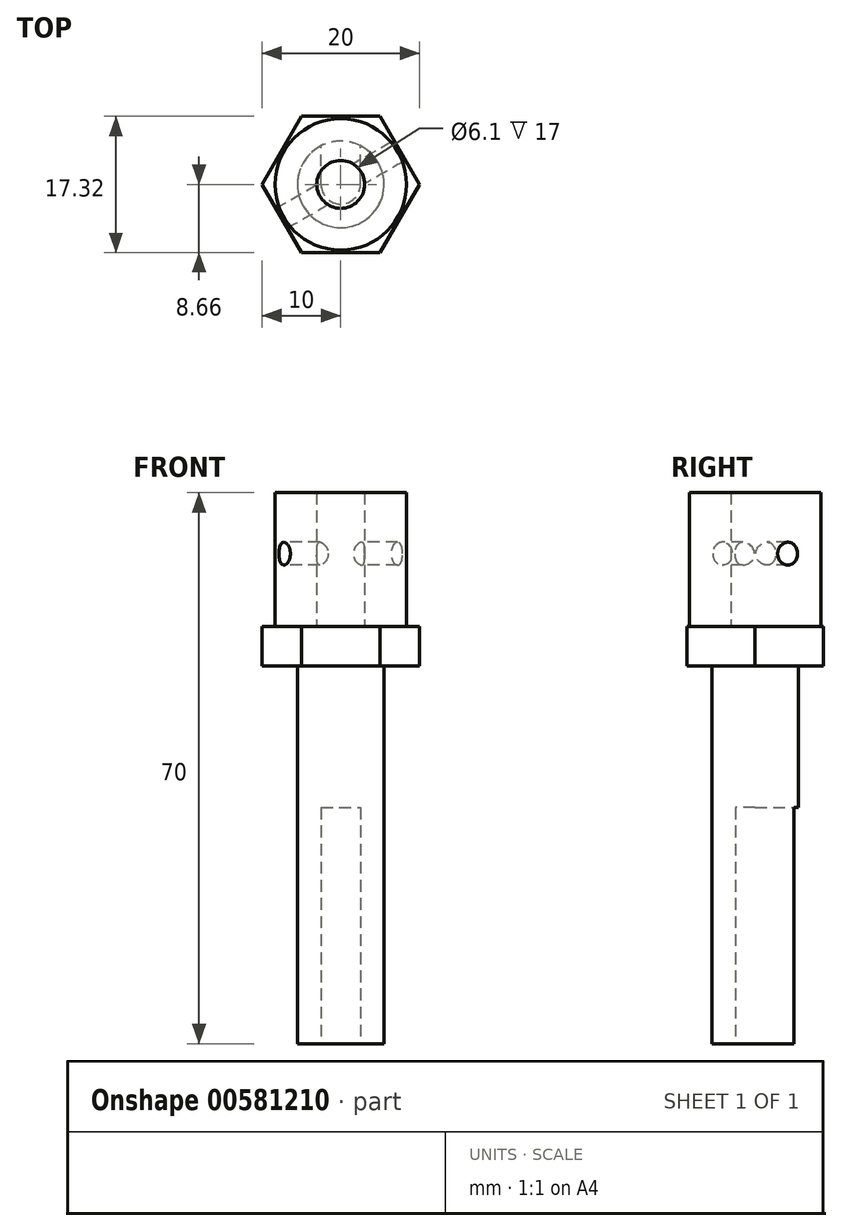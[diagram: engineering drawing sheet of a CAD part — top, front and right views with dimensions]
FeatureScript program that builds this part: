
annotation { "Feature Type Name" : "Feature", "Feature Type Description" : "" }
export const myFeature = defineFeature(function(context is Context, id is Id, definition is map)
    precondition{}
    {
        {
            var Q0;
            Q0=qCreatedBy(makeId("Top.planeOp"),FACE);
            var sketch = newSketch(context, id + "F0", { "sketchPlane" : qUnion([Q0])});
            skCircle(sketch, "E0.cCircle", {"center": v(0, 0) * mm, "radius": 8.66 * mm, "construction": true});
            skLineSegment(sketch, "E0.0", {"start": v(5, 8.66) * mm, "end": v(10, 0) * mm});
            skLineSegment(sketch, "E0.1", {"start": v(10, 0) * mm, "end": v(5, -8.66) * mm});
            skLineSegment(sketch, "E0.2", {"start": v(5, -8.66) * mm, "end": v(-5, -8.66) * mm});
            skLineSegment(sketch, "E0.3", {"start": v(-5, -8.66) * mm, "end": v(-10, 0) * mm});
            skLineSegment(sketch, "E0.4", {"start": v(-10, 0) * mm, "end": v(-5, 8.66) * mm});
            skLineSegment(sketch, "E0.5", {"start": v(-5, 8.66) * mm, "end": v(5, 8.66) * mm});
            skPoint(sketch, "E0.0.midPoint", {"position": v(7.5, 4.33) * mm});
            skSolve(sketch);
        }
        {
            var Q0;
            Q0=makeQuery(id+"F0.imprint","IMPRINT",FACE,{"disambiguationData":[TD([[makeQuery(id+"F0.imprint","IMPRINT",EDGE,{"derivedFrom":sQuery(id+"F0.wireOp",EDGE,"E0.0")}),-1.0]])]});
            extrude(context, id + "F1", {"entities" : qUnion([Q0]), "depth" : 5 * mm, "offsetDistance" : 25.4 * mm});
        }
        {
            var Q0;
            Q0=makeQuery(id+"F1.opExtrude","CAP_FACE",FACE,{"disambiguationData":[OSD([sQuery(id+"F0.wireOp",EDGE,"E0.0"),sQuery(id+"F0.wireOp",EDGE,"E0.1"),sQuery(id+"F0.wireOp",EDGE,"E0.2"),sQuery(id+"F0.wireOp",EDGE,"E0.3"),sQuery(id+"F0.wireOp",EDGE,"E0.4"),sQuery(id+"F0.wireOp",EDGE,"E0.5")])],"isStart":false});
            var sketch = newSketch(context, id + "F2", { "sketchPlane" : qUnion([Q0])});
            skCircle(sketch, "E1", {"center": v(0, 0) * mm, "radius": 8.35 * mm});
            skCircle(sketch, "E2", {"center": v(0, 0) * mm, "radius": 3.05 * mm});
            skSolve(sketch);
        }
        {
            var Q0;
            Q0=makeQuery(id+"F2.imprint","IMPRINT",FACE,{"disambiguationData":[TD([[makeQuery(id+"F2.imprint","IMPRINT",EDGE,{"derivedFrom":sQuery(id+"F2.wireOp",EDGE,"E1")}),1.0]])]});
            extrude(context, id + "F3", {"entities" : qUnion([Q0]), "operationType" : NewBodyOperationType.ADD, "depth" : 17 * mm, "offsetDistance" : 25.4 * mm});
        }
        {
            var Q0;
            Q0=makeQuery(id+"F1.opExtrude","SWEPT_FACE",FACE,{"disambiguationData":[OSD([sQuery(id+"F0.wireOp",EDGE,"E0.3")])]});
            var sketch = newSketch(context, id + "F4", { "sketchPlane" : qUnion([Q0])});
            skCircle(sketch, "E3", {"center": v(0, 14.25) * mm, "radius": 1.46 * mm});
            skSolve(sketch);
        }
        {
            var Q0;
            Q0 = qSketchRegion(id + "F4", true);
            extrude(context, id + "F5", {"entities" : qUnion([Q0]), "operationType" : NewBodyOperationType.REMOVE, "oppositeDirection" : true, "depth" : 25.4 * mm, "offsetDistance" : 25.4 * mm});
        }
        {
            var Q0;
            Q0=makeQuery(id+"F1.opExtrude","CAP_FACE",FACE,{"disambiguationData":[OSD([sQuery(id+"F0.wireOp",EDGE,"E0.0"),sQuery(id+"F0.wireOp",EDGE,"E0.1"),sQuery(id+"F0.wireOp",EDGE,"E0.2"),sQuery(id+"F0.wireOp",EDGE,"E0.3"),sQuery(id+"F0.wireOp",EDGE,"E0.4"),sQuery(id+"F0.wireOp",EDGE,"E0.5")])],"isStart":true});
            var sketch = newSketch(context, id + "F6", { "sketchPlane" : qUnion([Q0])});
            skCircle(sketch, "E4", {"center": v(0, 0) * mm, "radius": 5.5 * mm});
            skSolve(sketch);
        }
        {
            var Q0;
            Q0=makeQuery(id+"F6.imprint","IMPRINT",FACE,{"disambiguationData":[TD([[makeQuery(id+"F6.imprint","IMPRINT",EDGE,{"derivedFrom":sQuery(id+"F6.wireOp",EDGE,"E4")}),1.0]])]});
            extrude(context, id + "F7", {"entities" : qUnion([Q0]), "operationType" : NewBodyOperationType.ADD, "depth" : 48 * mm, "offsetDistance" : 25.4 * mm});
        }
        {
            var Q0;
            Q0=makeQuery(id+"F7.opExtrude","CAP_FACE",FACE,{"disambiguationData":[OSD([sQuery(id+"F6.wireOp",EDGE,"E4")])],"isStart":false});
            var sketch = newSketch(context, id + "F8", { "sketchPlane" : qUnion([Q0])});
            skArc(sketch, "E5", {"start": v(2.5, 0) * mm, "mid": v(0, 2.5) * mm, "end": v(-2.5, 0) * mm});
            skLineSegment(sketch, "E6", {"start": v(2.5, 0) * mm, "end": v(2.5, -4.9) * mm});
            skLineSegment(sketch, "E7", {"start": v(-2.5, 0) * mm, "end": v(-2.5, -4.9) * mm});
            skSolve(sketch);
        }
        {
            var Q0;
            Q0=makeQuery(id+"F8.imprint","IMPRINT",FACE,{"disambiguationData":[TD([[makeQuery(id+"F8.imprint","IMPRINT",EDGE,{"derivedFrom":sQuery(id+"F8.wireOp",EDGE,"E5")}),1.0]])]});
            extrude(context, id + "F9", {"entities" : qUnion([Q0]), "operationType" : NewBodyOperationType.REMOVE, "oppositeDirection" : true, "depth" : 30 * mm, "offsetDistance" : 25.4 * mm});
        }
    });
